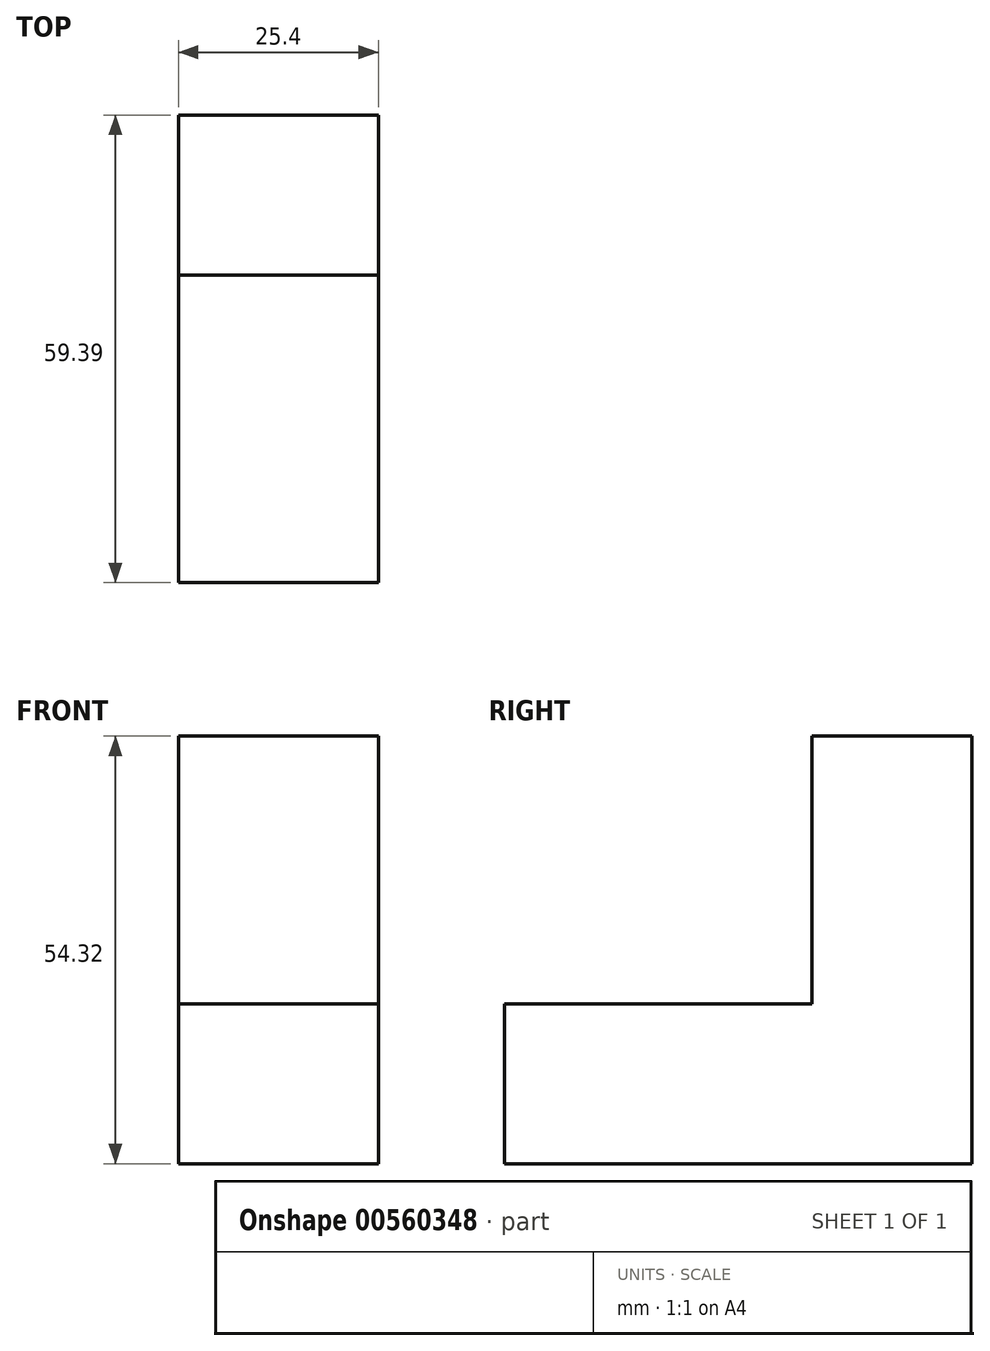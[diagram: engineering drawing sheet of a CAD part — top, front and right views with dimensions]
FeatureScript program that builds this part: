
annotation { "Feature Type Name" : "Feature", "Feature Type Description" : "" }
export const myFeature = defineFeature(function(context is Context, id is Id, definition is map)
    precondition{}
    {
        {
            var Q0;
            Q0=qCreatedBy(makeId("Right.planeOp"),FACE);
            var sketch = newSketch(context, id + "F0", { "sketchPlane" : qUnion([Q0])});
            skLineSegment(sketch, "E0", {"start": v(0, 0) * mm, "end": v(0, 54.32) * mm});
            skLineSegment(sketch, "E1", {"start": v(-20.32, 54.32) * mm, "end": v(0, 54.32) * mm});
            skLineSegment(sketch, "E2", {"start": v(-20.32, 54.32) * mm, "end": v(-20.32, 20.32) * mm});
            skLineSegment(sketch, "E3", {"start": v(-59.39, 20.32) * mm, "end": v(-20.32, 20.32) * mm});
            skLineSegment(sketch, "E4", {"start": v(-59.39, 20.32) * mm, "end": v(-59.39, 0) * mm});
            skLineSegment(sketch, "E5", {"start": v(0, 0) * mm, "end": v(-59.39, 0) * mm});
            skSolve(sketch);
        }
        {
            var Q0;
            Q0=makeQuery(id+"F0.imprint","IMPRINT",FACE,{"disambiguationData":[TD([[makeQuery(id+"F0.imprint","IMPRINT",EDGE,{"derivedFrom":sQuery(id+"F0.wireOp",EDGE,"E0")}),1.0]])]});
            extrude(context, id + "F1", {"entities" : qUnion([Q0]), "endBound" : BoundingType.SYMMETRIC, "depth" : 25.4 * mm, "offsetDistance" : 25.4 * mm});
        }
        {
            var Q0;
            Q0=qCreatedBy(makeId("Right.planeOp"),FACE);
            cPlane(context, id + "F2", {"entities" : qUnion([Q0]), "cplaneType" : CPlaneType.OFFSET, "offset" : 8.7 * mm, "width" : 152.4 * mm, "height" : 152.4 * mm});
        }
    });
